# Revit family: Table-Teknion-Zones_ZNTLT-Laptop_Table-R2019
name_source: partatom
category: Furniture
units: mm (PartAtom-declared; Revit-internal decimal feet)

## family parameters
Always vertical = Yes
Cut with Voids When Loaded = No
OmniClass Number = 23.40.70.14.64.21
OmniClass Title = Systems Furniture
Room Calculation Point = No
Shared = Yes
Work Plane-Based = No

## types (1)
- Laptop Table
    Assembly Code = E2020200
    Depth = 11"
    Description = Laptop Table
    Height = 26"
    Manufacturer = Teknion
    Manufacturer Fax = 416.661.4586
    Model = ZNTLT261133
    Part Number = ZNTLT
    Product Documentation Link = https://www.teknion.com
    Product Line = Zones
    Product Page URL = http://www.teknion.com
    Series = Zones
    Sustainability Data = http://www.teknion.com
    URL = http://www.teknion.com
    Warranty = http://www.teknion.com
    Width = 33"

## geometry (parser evidence)
native form markers: Sweep x3
no freeform markers — native parametric forms only
